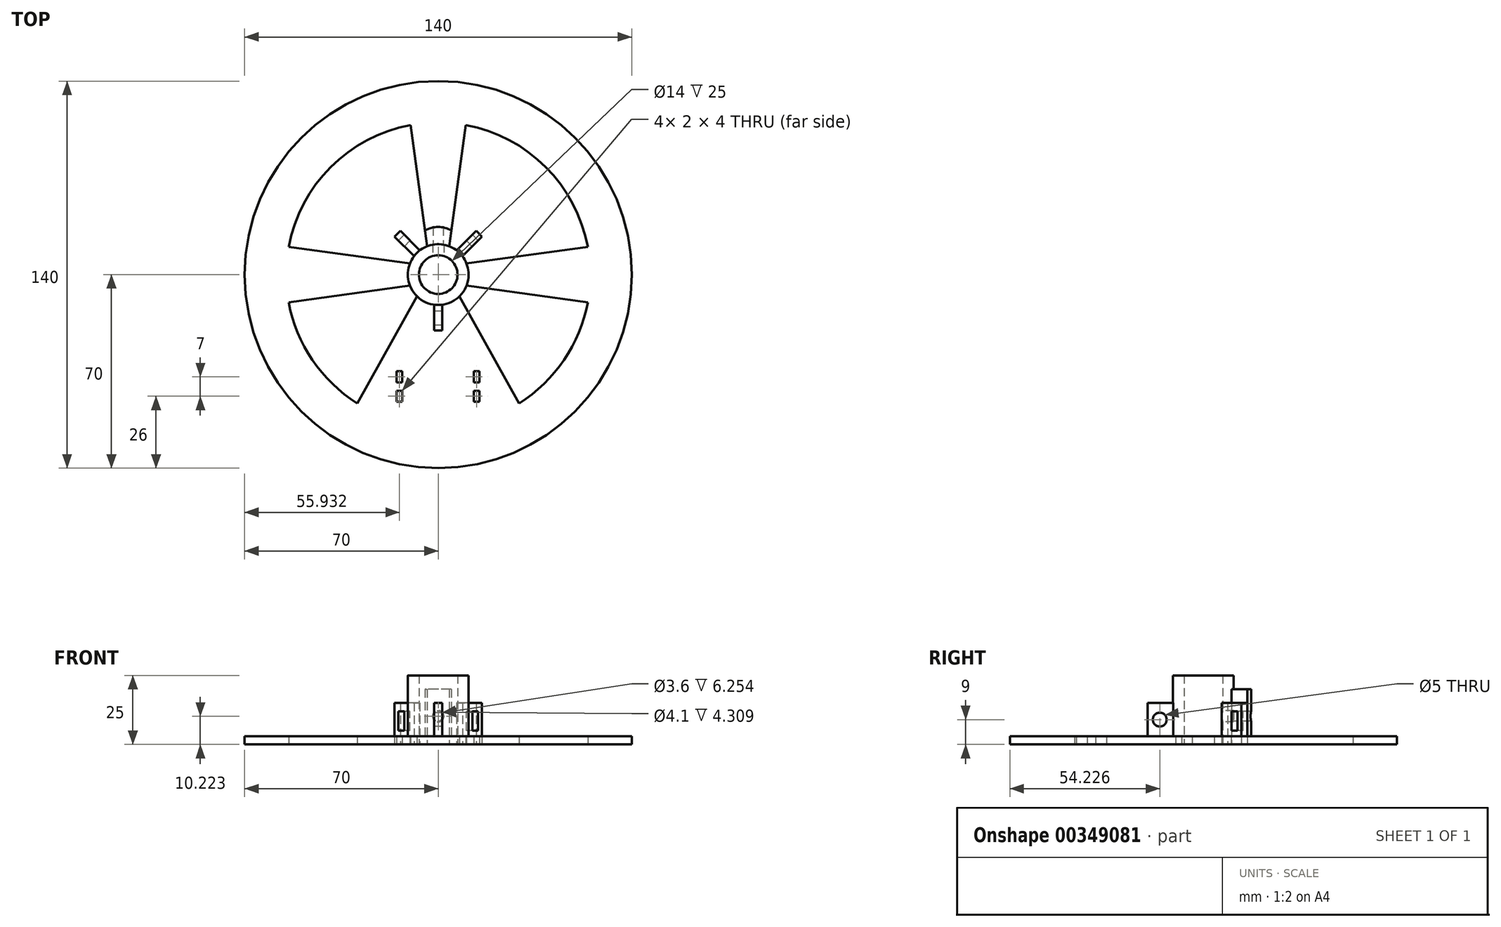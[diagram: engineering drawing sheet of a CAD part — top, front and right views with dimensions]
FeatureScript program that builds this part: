
annotation { "Feature Type Name" : "Feature", "Feature Type Description" : "" }
export const myFeature = defineFeature(function(context is Context, id is Id, definition is map)
    precondition{}
    {
        {
            var Q0;
            Q0=qCreatedBy(makeId("Top.planeOp"),FACE);
            var sketch = newSketch(context, id + "F0", { "sketchPlane" : qUnion([Q0])});
            skLineSegment(sketch, "E0", {"start": v(0, 0) * mm, "end": v(57.07, 57.07) * mm, "construction": true});
            skLineSegment(sketch, "E1", {"start": v(0, 0) * mm, "end": v(-61.62, 61.62) * mm, "construction": true});
            skLineSegment(sketch, "E2", {"start": v(0, 0) * mm, "end": v(0, -74.2) * mm, "construction": true});
            skArc(sketch, "E3", {"start": v(-39, 58.14) * mm, "mid": v(-49.5, 49.5) * mm, "end": v(-58.14, 39) * mm});
            skArc(sketch, "E4", {"start": v(-58.14, 39) * mm, "mid": v(49.5, -49.5) * mm, "end": v(-39, 58.14) * mm});
            skCircle(sketch, "E5", {"center": v(0, 0) * mm, "radius": 7 * mm});
            skCircle(sketch, "E6", {"center": v(0, 0) * mm, "radius": 11 * mm});
            skArc(sketch, "E7.2.1", {"start": v(67.96, 16.76) * mm, "mid": v(65.78, 23.94) * mm, "end": v(62.83, 30.85) * mm});
            skCircle(sketch, "E8", {"center": v(0, 0) * mm, "radius": 55 * mm});
            skLineSegment(sketch, "E9", {"start": v(0, 71.1) * mm, "end": v(0, -3.57) * mm, "construction": true});
            skLineSegment(sketch, "E10", {"start": v(-10, 54.08) * mm, "end": v(-4, 10.25) * mm});
            skLineSegment(sketch, "E11", {"start": v(10, 54.08) * mm, "end": v(4, 10.25) * mm});
            skLineSegment(sketch, "E12.1.0", {"start": v(-54.08, 10) * mm, "end": v(-10.25, 4) * mm});
            skLineSegment(sketch, "E12.1.1", {"start": v(-54.08, -10) * mm, "end": v(-10.25, -4) * mm});
            skLineSegment(sketch, "E12.3.0", {"start": v(54.08, -10) * mm, "end": v(10.25, -4) * mm});
            skLineSegment(sketch, "E12.3.1", {"start": v(54.08, 10) * mm, "end": v(10.25, 4) * mm});
            skArc(sketch, "E13", {"start": v(4.77, 15.87) * mm, "mid": v(0, 17.25) * mm, "end": v(-4.77, 15.87) * mm});
            skLineSegment(sketch, "E14", {"start": v(-1.5, -10.9) * mm, "end": v(-1.5, -20.16) * mm});
            skLineSegment(sketch, "E15", {"start": v(-1.5, -20.16) * mm, "end": v(1.5, -20.16) * mm});
            skLineSegment(sketch, "E16", {"start": v(1.5, -20.16) * mm, "end": v(1.5, -10.9) * mm});
            skLineSegment(sketch, "E17.bottom", {"start": v(-15.07, -35) * mm, "end": v(-13.07, -35) * mm});
            skLineSegment(sketch, "E17.top", {"start": v(-15.07, -39) * mm, "end": v(-13.07, -39) * mm});
            skLineSegment(sketch, "E17.left", {"start": v(-15.07, -35) * mm, "end": v(-15.07, -39) * mm});
            skLineSegment(sketch, "E17.right", {"start": v(-13.07, -35) * mm, "end": v(-13.07, -39) * mm});
            skLineSegment(sketch, "E18.bottom", {"start": v(12.93, -35) * mm, "end": v(14.93, -35) * mm});
            skLineSegment(sketch, "E18.top", {"start": v(12.93, -39) * mm, "end": v(14.93, -39) * mm});
            skLineSegment(sketch, "E18.left", {"start": v(12.93, -35) * mm, "end": v(12.93, -39) * mm});
            skLineSegment(sketch, "E18.right", {"start": v(14.93, -35) * mm, "end": v(14.93, -39) * mm});
            skLineSegment(sketch, "E19", {"start": v(-18.61, -37) * mm, "end": v(20.4, -37) * mm, "construction": true});
            skLineSegment(sketch, "E20.bottom", {"start": v(-15.07, -42) * mm, "end": v(-13.07, -42) * mm});
            skLineSegment(sketch, "E20.top", {"start": v(-15.07, -46) * mm, "end": v(-13.07, -46) * mm});
            skLineSegment(sketch, "E20.left", {"start": v(-15.07, -42) * mm, "end": v(-15.07, -46) * mm});
            skLineSegment(sketch, "E20.right", {"start": v(-13.07, -42) * mm, "end": v(-13.07, -46) * mm});
            skLineSegment(sketch, "E21.bottom", {"start": v(12.93, -42) * mm, "end": v(14.93, -42) * mm});
            skLineSegment(sketch, "E21.top", {"start": v(12.93, -46) * mm, "end": v(14.93, -46) * mm});
            skLineSegment(sketch, "E21.left", {"start": v(12.93, -42) * mm, "end": v(12.93, -46) * mm});
            skLineSegment(sketch, "E21.right", {"start": v(14.93, -42) * mm, "end": v(14.93, -46) * mm});
            skLineSegment(sketch, "E22", {"start": v(-18.62, -44) * mm, "end": v(19.75, -44) * mm, "construction": true});
            skLineSegment(sketch, "E23", {"start": v(-14.07, -36.98) * mm, "end": v(-14.07, -57.94) * mm, "construction": true});
            skPoint(sketch, "E23.startSnap0", {"position": v(-14.07, -35) * mm});
            skLineSegment(sketch, "E24", {"start": v(-7.65, -7.9) * mm, "end": v(-29.25, -46.57) * mm});
            skLineSegment(sketch, "E25", {"start": v(7.65, -7.9) * mm, "end": v(29.25, -46.57) * mm});
            skLineSegment(sketch, "E26", {"start": v(-8.77, 6.64) * mm, "end": v(-15.84, 13.72) * mm});
            skLineSegment(sketch, "E27", {"start": v(-15.84, 13.72) * mm, "end": v(-13.72, 15.84) * mm});
            skLineSegment(sketch, "E28", {"start": v(-13.72, 15.84) * mm, "end": v(-6.64, 8.77) * mm});
            skLineSegment(sketch, "E29", {"start": v(6.64, 8.77) * mm, "end": v(13.72, 15.84) * mm});
            skLineSegment(sketch, "E30", {"start": v(13.72, 15.84) * mm, "end": v(15.84, 13.72) * mm});
            skLineSegment(sketch, "E31", {"start": v(15.84, 13.72) * mm, "end": v(8.77, 6.64) * mm});
            skSolve(sketch);
        }
        {
            var Q0;
            Q0=makeQuery(id+"F0.imprint","IMPRINT",FACE,{"disambiguationData":[TD([[makeQuery(id+"F0.imprint","IMPRINT",EDGE,{"derivedFrom":sQuery(id+"F0.wireOp",EDGE,"E3")}),1.0]])]});
            var Q1;
            Q1=makeQuery(id+"F0.imprint","IMPRINT",FACE,{"disambiguationData":[TD([[makeQuery(id+"F0.imprint","IMPRINT",EDGE,{"derivedFrom":sQuery(id+"F0.wireOp",EDGE,"a568e6f3-4b71-4480-842e-13f098c67c3a1")}),1.0]])]});
            var Q2;
            Q2=makeQuery(id+"F0.imprint","IMPRINT",FACE,{"disambiguationData":[TD([[makeQuery(id+"F0.imprint","IMPRINT",EDGE,{"derivedFrom":sQuery(id+"F0.wireOp",EDGE,"E4")}),1.0]])]});
            var Q3;
            {var subQ0=sQuery(id+"F0.wireOp",EDGE,"E12.1.0");Q3=makeQuery(id+"F0.imprint","IMPRINT",FACE,{"disambiguationData":[TD([[makeQuery(id+"F0.imprint","IMPRINT",EDGE,{"derivedFrom":subQ0}),-1.0]])]});}
            var Q4;
            {var subQ0=sQuery(id+"F0.wireOp",EDGE,"E10");Q4=makeQuery(id+"F0.imprint","IMPRINT",FACE,{"disambiguationData":[TD([[makeQuery(id+"F0.imprint","IMPRINT",EDGE,{"derivedFrom":subQ0}),1.0]])]});}
            var Q5;
            {var subQ0=sQuery(id+"F0.wireOp",EDGE,"E12.3.0");Q5=makeQuery(id+"F0.imprint","IMPRINT",FACE,{"disambiguationData":[TD([[makeQuery(id+"F0.imprint","IMPRINT",EDGE,{"derivedFrom":subQ0}),-1.0]])]});}
            var Q6;
            {var subQ0=sQuery(id+"F0.wireOp",EDGE,"E12.2.0");Q6=makeQuery(id+"F0.imprint","IMPRINT",FACE,{"disambiguationData":[TD([[makeQuery(id+"F0.imprint","IMPRINT",EDGE,{"derivedFrom":subQ0}),-1.0]])]});}
            var Q7;
            Q7=makeQuery(id+"F0.imprint","IMPRINT",FACE,{"disambiguationData":[TD([[makeQuery(id+"F0.imprint","IMPRINT",EDGE,{"derivedFrom":sQuery(id+"F0.wireOp",EDGE,"DxC1QGky-HRrN-gzPb-Pb88-aNf4S9f9K86J.bottom")}),1.0]])]});
            var Q8;
            {var subQ0=sQuery(id+"F0.wireOp",EDGE,"E14");Q8=makeQuery(id+"F0.imprint","IMPRINT",FACE,{"disambiguationData":[TD([[makeQuery(id+"F0.imprint","IMPRINT",EDGE,{"derivedFrom":subQ0}),-1.0]])]});}
            extrude(context, id + "F1", {"entities" : qUnion([Q0, Q1, Q2, Q3, Q4, Q5, Q6, Q7, Q8]), "depth" : 3 * mm});
        }
        {
            var Q0;
            Q0=qCreatedBy(makeId("Right.planeOp"),FACE);
            var sketch = newSketch(context, id + "F2", { "sketchPlane" : qUnion([Q0])});
            skLineSegment(sketch, "E32", {"start": v(0, 42.43) * mm, "end": v(0, -20.95) * mm, "construction": true});
            skSolve(sketch);
        }
        {
            var Q0;
            Q0=makeQuery(id+"F0.imprint","IMPRINT",FACE,{"disambiguationData":[TD([[makeQuery(id+"F0.imprint","IMPRINT",EDGE,{"derivedFrom":sQuery(id+"F0.wireOp",EDGE,"E5")}),-1.0]])]});
            extrude(context, id + "F3", {"entities" : qUnion([Q0]), "operationType" : NewBodyOperationType.ADD, "depth" : 25 * mm});
        }
        {
            var Q0;
            {var subQ5=sQuery(id+"F0.wireOp",EDGE,"E13");Q0=makeQuery(id+"F0.imprint","IMPRINT",FACE,{"disambiguationData":[TD([[makeQuery(id+"F0.imprint","IMPRINT",EDGE,{"derivedFrom":subQ5}),1.0]])]});}
            extrude(context, id + "F4", {"entities" : qUnion([Q0]), "operationType" : NewBodyOperationType.ADD, "depth" : 20 * mm});
        }
        {
            var Q0;
            {var subQ0=sQuery(id+"F0.wireOp",EDGE,"E26");Q0=makeQuery(id+"F0.imprint","IMPRINT",FACE,{"disambiguationData":[TD([[makeQuery(id+"F0.imprint","IMPRINT",EDGE,{"derivedFrom":subQ0}),-1.0]])]});}
            var Q1;
            {var subQ0=sQuery(id+"F0.wireOp",EDGE,"E29");Q1=makeQuery(id+"F0.imprint","IMPRINT",FACE,{"disambiguationData":[TD([[makeQuery(id+"F0.imprint","IMPRINT",EDGE,{"derivedFrom":subQ0}),-1.0]])]});}
            var Q2;
            {var subQ0=sQuery(id+"F0.wireOp",EDGE,"E14");Q2=makeQuery(id+"F0.imprint","IMPRINT",FACE,{"disambiguationData":[TD([[makeQuery(id+"F0.imprint","IMPRINT",EDGE,{"derivedFrom":subQ0}),1.0]])]});}
            extrude(context, id + "F5", {"entities" : qUnion([Q0, Q1, Q2]), "operationType" : NewBodyOperationType.ADD, "depth" : 15 * mm});
        }
        {
            var Q0;
            Q0=makeQuery(id+"F5.opExtrude","SWEPT_FACE",FACE,{"disambiguationData":[OSD([sQuery(id+"F0.wireOp",EDGE,"E26")])]});
            var sketch = newSketch(context, id + "F6", { "sketchPlane" : qUnion([Q0])});
            skLineSegment(sketch, "E33.bottom", {"start": v(-18.9, 12) * mm, "end": v(-15.9, 12) * mm});
            skLineSegment(sketch, "E33.top", {"start": v(-18.9, 5) * mm, "end": v(-15.9, 5) * mm});
            skLineSegment(sketch, "E33.left", {"start": v(-18.9, 12) * mm, "end": v(-18.9, 5) * mm});
            skLineSegment(sketch, "E33.right", {"start": v(-15.9, 12) * mm, "end": v(-15.9, 5) * mm});
            skSolve(sketch);
        }
        {
            var Q0;
            Q0=makeQuery(id+"F6.imprint","IMPRINT",FACE,{"disambiguationData":[TD([[makeQuery(id+"F6.imprint","IMPRINT",EDGE,{"derivedFrom":sQuery(id+"F6.wireOp",EDGE,"E33.bottom")}),-1.0]])]});
            extrude(context, id + "F7", {"entities" : qUnion([Q0]), "operationType" : NewBodyOperationType.REMOVE, "oppositeDirection" : true, "depth" : 25 * mm});
        }
        {
            var Q0;
            Q0=makeQuery(id+"F5.opExtrude","SWEPT_FACE",FACE,{"disambiguationData":[OSD([sQuery(id+"F0.wireOp",EDGE,"E31")])]});
            var sketch = newSketch(context, id + "F8", { "sketchPlane" : qUnion([Q0])});
            skLineSegment(sketch, "E34.bottom", {"start": v(15.9, 12) * mm, "end": v(18.9, 12) * mm});
            skLineSegment(sketch, "E34.top", {"start": v(15.9, 5) * mm, "end": v(18.9, 5) * mm});
            skLineSegment(sketch, "E34.left", {"start": v(15.9, 12) * mm, "end": v(15.9, 5) * mm});
            skLineSegment(sketch, "E34.right", {"start": v(18.9, 12) * mm, "end": v(18.9, 5) * mm});
            skSolve(sketch);
        }
        {
            var Q0;
            Q0=makeQuery(id+"F8.imprint","IMPRINT",FACE,{"disambiguationData":[TD([[makeQuery(id+"F8.imprint","IMPRINT",EDGE,{"derivedFrom":sQuery(id+"F8.wireOp",EDGE,"E34.bottom")}),-1.0]])]});
            extrude(context, id + "F9", {"entities" : qUnion([Q0]), "operationType" : NewBodyOperationType.REMOVE, "oppositeDirection" : true, "depth" : 25 * mm});
        }
        {
            var Q0;
            Q0=sQuery(id+"F2.wireOp",EDGE,"E32");
            cPlane(context, id + "F10", {"entities" : qUnion([Q0]), "cplaneType" : CPlaneType.LINE_ANGLE, "offset" : 25 * mm, "angle" : 90 * degree, "width" : 150 * mm, "height" : 150 * mm});
        }
        {
            var Q0;
            Q0=qCreatedBy(id+"F10.planeOp",FACE);
            var sketch = newSketch(context, id + "F11", { "sketchPlane" : qUnion([Q0])});
            skCircle(sketch, "E35", {"center": v(0, 10.22) * mm, "radius": 1 * mm});
            skSolve(sketch);
        }
        {
            var Q0;
            Q0=sQuery(id+"F11.wireOp",VERTEX,"E35.center");
            var Q1;
            Q1=makeQuery(id+"F1.opExtrude","SWEPT_BODY",BODY,{"disambiguationData":[OSD([sQuery(id+"F0.wireOp",EDGE,"E3"),sQuery(id+"F0.wireOp",EDGE,"E4"),sQuery(id+"F0.wireOp",EDGE,"E6"),sQuery(id+"F0.wireOp",EDGE,"E7.1.0"),sQuery(id+"F0.wireOp",EDGE,"E7.1.2"),sQuery(id+"F0.wireOp",EDGE,"E7.1.3"),sQuery(id+"F0.wireOp",EDGE,"E7.2.0"),sQuery(id+"F0.wireOp",EDGE,"E7.2.2"),sQuery(id+"F0.wireOp",EDGE,"E7.2.3"),sQuery(id+"F0.wireOp",EDGE,"E8"),sQuery(id+"F0.wireOp",EDGE,"E10"),sQuery(id+"F0.wireOp",EDGE,"E11"),sQuery(id+"F0.wireOp",EDGE,"E12.1.0"),sQuery(id+"F0.wireOp",EDGE,"E12.1.1"),sQuery(id+"F0.wireOp",EDGE,"E12.3.0"),sQuery(id+"F0.wireOp",EDGE,"E12.3.1"),sQuery(id+"F0.wireOp",EDGE,"DxC1QGky-HRrN-gzPb-Pb88-aNf4S9f9K86J.bottom"),sQuery(id+"F0.wireOp",EDGE,"DxC1QGky-HRrN-gzPb-Pb88-aNf4S9f9K86J.top"),sQuery(id+"F0.wireOp",EDGE,"DxC1QGky-HRrN-gzPb-Pb88-aNf4S9f9K86J.left"),sQuery(id+"F0.wireOp",EDGE,"DxC1QGky-HRrN-gzPb-Pb88-aNf4S9f9K86J.right"),sQuery(id+"F0.wireOp",EDGE,"2d52bbff-8edd-4f97-a77e-c5ac5676539f0.MirrorCS"),sQuery(id+"F0.wireOp",EDGE,"2d52bbff-8edd-4f97-a77e-c5ac5676539f1.MirrorCS"),sQuery(id+"F0.wireOp",EDGE,"2d52bbff-8edd-4f97-a77e-c5ac5676539f3.MirrorCS"),sQuery(id+"F0.wireOp",EDGE,"2d52bbff-8edd-4f97-a77e-c5ac5676539f6.MirrorCS"),sQuery(id+"F0.wireOp",EDGE,"9be3de77-d5e6-4486-93f5-ee3b1d01e160.bottom"),sQuery(id+"F0.wireOp",EDGE,"9be3de77-d5e6-4486-93f5-ee3b1d01e160.top"),sQuery(id+"F0.wireOp",EDGE,"9be3de77-d5e6-4486-93f5-ee3b1d01e160.left"),sQuery(id+"F0.wireOp",EDGE,"9be3de77-d5e6-4486-93f5-ee3b1d01e160.right"),sQuery(id+"F0.wireOp",EDGE,"a1a42e55-1d56-4dcf-bef6-dfa0cd09f213.MirrorCS"),sQuery(id+"F0.wireOp",EDGE,"69599f0c-71d3-4e93-93c2-72b703701d98.MirrorCS"),sQuery(id+"F0.wireOp",EDGE,"1db623de-f78b-4af5-8506-0e3137d38347.MirrorCS"),sQuery(id+"F0.wireOp",EDGE,"2d571f0c-88a3-41e3-b531-1a1a6e09f5e6.MirrorCS"),sQuery(id+"F0.wireOp",EDGE,"QAUAg4Rv-rJLO-vGMV-bjQP-bpTTJf4zCCb9"),sQuery(id+"F0.wireOp",EDGE,"6e9785c6-ce13-4db9-ba87-197f2c4649aa0.MirrorCS")])]});
            hole(context, id + "F12", {"style" : HoleStyle.C_BORE, "endStyle" : HoleEndStyle.THROUGH, "oppositeDirection" : true, "holeDiameter" : 3.6 * mm, "cBoreDiameter" : 4.1 * mm, "cBoreDepth" : 11 * mm, "isTappedThrough" : true, "tappedDepth" : 12 * mm, "tapClearance" : 3, "startFromSketch" : true, "locations" : qUnion([Q0]), "scope" : qUnion([Q1])});
        }
        {
            var Q0;
            Q0=makeQuery(id+"F5.opExtrude","SWEPT_FACE",FACE,{"disambiguationData":[OSD([sQuery(id+"F0.wireOp",EDGE,"E14")])]});
            var sketch = newSketch(context, id + "F13", { "sketchPlane" : qUnion([Q0])});
            skLineSegment(sketch, "E36", {"start": v(15.77, 17.78) * mm, "end": v(15.77, -3.48) * mm, "construction": true});
            skPoint(sketch, "E36.startSnap0", {"position": v(15.77, 15) * mm});
            skCircle(sketch, "E37", {"center": v(15.77, 9) * mm, "radius": 2.5 * mm});
            skLineSegment(sketch, "E38.0.1", {"start": v(10.9, 3) * mm, "end": v(20.16, 3) * mm});
            skLineSegment(sketch, "E38.0.3", {"start": v(20.16, 15) * mm, "end": v(10.9, 15) * mm});
            skPoint(sketch, "E39", {"position": v(10.9, 9) * mm});
            skSolve(sketch);
        }
        {
            var Q0;
            Q0=qSketchRegion(id+"F13",true);
            extrude(context, id + "F14", {"entities" : qUnion([Q0]), "operationType" : NewBodyOperationType.REMOVE, "oppositeDirection" : true, "depth" : 25 * mm});
        }
    });
